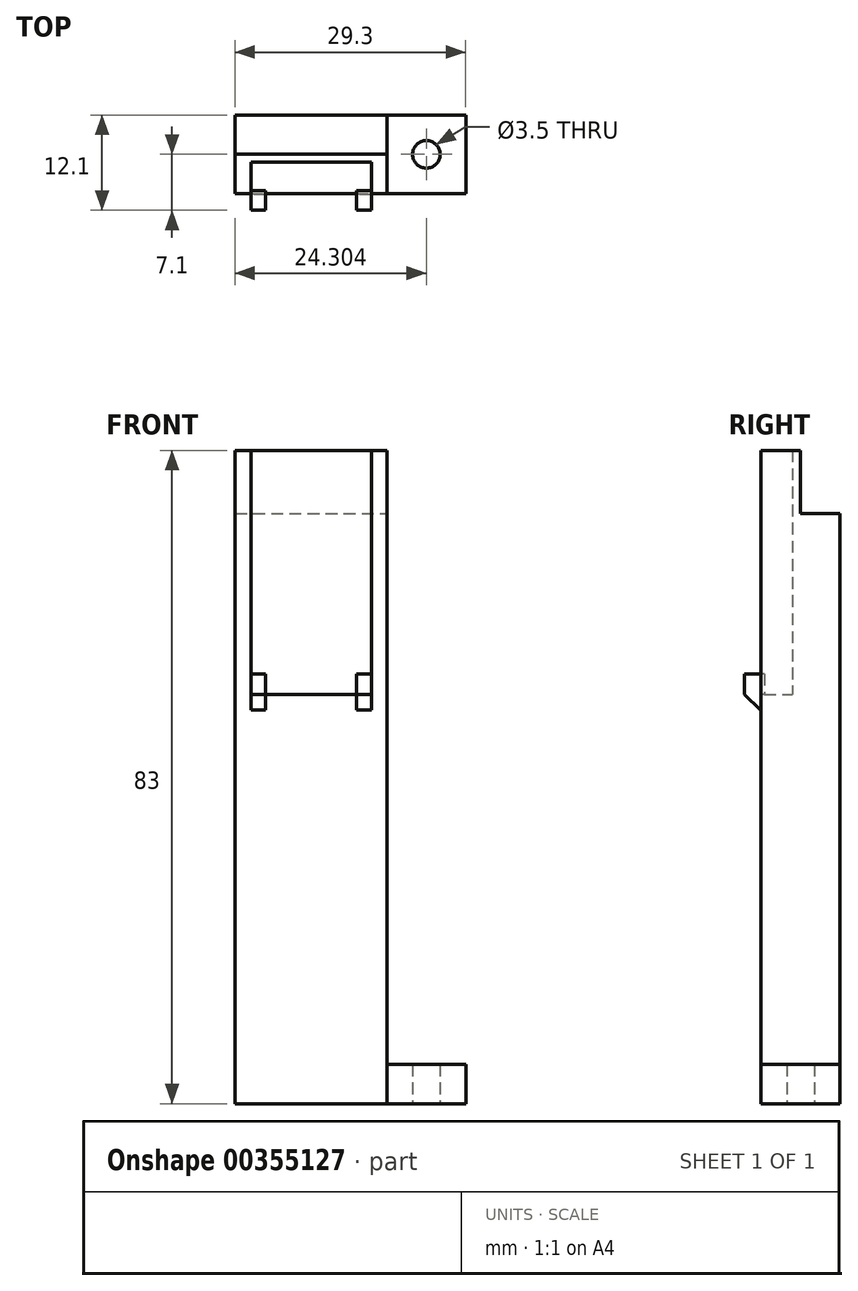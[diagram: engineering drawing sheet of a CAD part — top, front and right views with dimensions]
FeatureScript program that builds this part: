
annotation { "Feature Type Name" : "Feature", "Feature Type Description" : "" }
export const myFeature = defineFeature(function(context is Context, id is Id, definition is map)
    precondition{}
    {
        {
            var Q0;
            Q0=qCreatedBy(makeId("Front.planeOp"),FACE);
            var sketch = newSketch(context, id + "F0", { "sketchPlane" : qUnion([Q0])});
            skLineSegment(sketch, "E0.bottom", {"start": v(-6.93, -11.62) * mm, "end": v(8.37, -11.62) * mm});
            skLineSegment(sketch, "E0.top", {"start": v(-6.93, -42.62) * mm, "end": v(8.37, -42.62) * mm});
            skLineSegment(sketch, "E0.left", {"start": v(-6.93, -11.62) * mm, "end": v(-6.93, -42.62) * mm});
            skLineSegment(sketch, "E0.right", {"start": v(8.37, -11.62) * mm, "end": v(8.37, -42.62) * mm});
            skLineSegment(sketch, "E1.0", {"start": v(-8.93, -11.62) * mm, "end": v(-8.93, -44.62) * mm});
            skLineSegment(sketch, "E1.1", {"start": v(-8.93, -44.62) * mm, "end": v(10.37, -44.62) * mm});
            skLineSegment(sketch, "E1.2", {"start": v(10.37, -11.62) * mm, "end": v(10.37, -44.62) * mm});
            skLineSegment(sketch, "E2", {"start": v(-8.93, -11.62) * mm, "end": v(-6.93, -11.62) * mm});
            skLineSegment(sketch, "E3", {"start": v(8.37, -11.62) * mm, "end": v(10.37, -11.62) * mm});
            skSolve(sketch);
        }
        {
            var Q0;
            Q0=makeQuery(id+"F0.imprint","IMPRINT",FACE,{"disambiguationData":[TD([[makeQuery(id+"F0.imprint","IMPRINT",EDGE,{"derivedFrom":sQuery(id+"F0.wireOp",EDGE,"E0.bottom")}),-1.0]])]});
            extrude(context, id + "F1", {"entities" : qUnion([Q0]), "depth" : 1 * mm});
        }
        {
            var Q0;
            Q0=makeQuery(id+"F0.imprint","IMPRINT",FACE,{"disambiguationData":[TD([[makeQuery(id+"F0.imprint","IMPRINT",EDGE,{"derivedFrom":sQuery(id+"F0.wireOp",EDGE,"E0.top")}),-1.0]])]});
            extrude(context, id + "F2", {"entities" : qUnion([Q0]), "operationType" : NewBodyOperationType.ADD, "depth" : 5 * mm});
        }
        {
            var Q0;
            Q0=makeQuery(id+"F2.opExtrude","SWEPT_FACE",FACE,{"disambiguationData":[OSD([sQuery(id+"F0.wireOp",EDGE,"E0.top")])]});
            var sketch = newSketch(context, id + "F3", { "sketchPlane" : qUnion([Q0])});
            skLineSegment(sketch, "E4", {"start": v(0.72, -5) * mm, "end": v(0.72, -1) * mm, "construction": true});
            skLineSegment(sketch, "E5.bottom", {"start": v(8.37, -4.6) * mm, "end": v(6.47, -4.6) * mm});
            skLineSegment(sketch, "E5.top", {"start": v(8.37, -7.1) * mm, "end": v(6.47, -7.1) * mm});
            skLineSegment(sketch, "E5.left", {"start": v(8.37, -4.6) * mm, "end": v(8.37, -7.1) * mm});
            skLineSegment(sketch, "E5.right", {"start": v(6.47, -4.6) * mm, "end": v(6.47, -7.1) * mm});
            skLineSegment(sketch, "E6.MirrorCS", {"start": v(-5.03, -4.6) * mm, "end": v(-5.03, -7.1) * mm});
            skLineSegment(sketch, "E7.MirrorCS", {"start": v(-6.93, -4.6) * mm, "end": v(-5.03, -4.6) * mm});
            skLineSegment(sketch, "E8.MirrorCS", {"start": v(-6.93, -4.6) * mm, "end": v(-6.93, -7.1) * mm});
            skLineSegment(sketch, "E9.MirrorCS", {"start": v(-6.93, -7.1) * mm, "end": v(-5.03, -7.1) * mm});
            skSolve(sketch);
        }
        {
            var Q0;
            {var subQ0=sQuery(id+"F3.wireOp",EDGE,"E9.MirrorCS");Q0=makeQuery(id+"F3.imprint","IMPRINT",FACE,{"disambiguationData":[TD([[makeQuery(id+"F3.imprint","IMPRINT",EDGE,{"derivedFrom":subQ0}),1.0]])]});}
            var Q1;
            {var subQ0=sQuery(id+"F3.wireOp",EDGE,"E7.MirrorCS");Q1=makeQuery(id+"F3.imprint","IMPRINT",FACE,{"disambiguationData":[TD([[makeQuery(id+"F3.imprint","IMPRINT",EDGE,{"derivedFrom":subQ0}),-1.0]])]});}
            var Q2;
            {var subQ0=sQuery(id+"F3.wireOp",EDGE,"E5.top");Q2=makeQuery(id+"F3.imprint","IMPRINT",FACE,{"disambiguationData":[TD([[makeQuery(id+"F3.imprint","IMPRINT",EDGE,{"derivedFrom":subQ0}),-1.0]])]});}
            var Q3;
            {var subQ0=sQuery(id+"F3.wireOp",EDGE,"E5.bottom");Q3=makeQuery(id+"F3.imprint","IMPRINT",FACE,{"disambiguationData":[TD([[makeQuery(id+"F3.imprint","IMPRINT",EDGE,{"derivedFrom":subQ0}),1.0]])]});}
            extrude(context, id + "F4", {"entities" : qUnion([Q0, Q1, Q2, Q3]), "operationType" : NewBodyOperationType.ADD, "depth" : 2.6 * mm});
        }
        {
            var Q0;
            Q0=makeQuery(id+"F2.opExtrude","CAP_FACE",FACE,{"disambiguationData":[OSD([sQuery(id+"F0.wireOp",EDGE,"E0.top"),sQuery(id+"F0.wireOp",EDGE,"E0.left"),sQuery(id+"F0.wireOp",EDGE,"E0.right"),sQuery(id+"F0.wireOp",EDGE,"E1.0"),sQuery(id+"F0.wireOp",EDGE,"E1.1"),sQuery(id+"F0.wireOp",EDGE,"E1.2"),sQuery(id+"F0.wireOp",EDGE,"E2"),sQuery(id+"F0.wireOp",EDGE,"E3")])],"isStart":false});
            var sketch = newSketch(context, id + "F5", { "sketchPlane" : qUnion([Q0])});
            skLineSegment(sketch, "E10.bottom", {"start": v(6.47, -42.62) * mm, "end": v(8.37, -42.62) * mm});
            skLineSegment(sketch, "E10.top", {"start": v(6.47, -44.62) * mm, "end": v(8.37, -44.62) * mm});
            skLineSegment(sketch, "E10.left", {"start": v(6.47, -42.62) * mm, "end": v(6.47, -44.62) * mm});
            skLineSegment(sketch, "E10.right", {"start": v(8.37, -42.62) * mm, "end": v(8.37, -44.62) * mm});
            skLineSegment(sketch, "E11.bottom", {"start": v(-6.93, -42.62) * mm, "end": v(-5.03, -42.62) * mm});
            skLineSegment(sketch, "E11.top", {"start": v(-6.93, -44.62) * mm, "end": v(-5.03, -44.62) * mm});
            skLineSegment(sketch, "E11.left", {"start": v(-6.93, -42.62) * mm, "end": v(-6.93, -44.62) * mm});
            skLineSegment(sketch, "E11.right", {"start": v(-5.03, -42.62) * mm, "end": v(-5.03, -44.62) * mm});
            skSolve(sketch);
        }
        {
            var Q0;
            Q0=makeQuery(id+"F5.imprint","IMPRINT",FACE,{"disambiguationData":[TD([[makeQuery(id+"F5.imprint","IMPRINT",EDGE,{"derivedFrom":sQuery(id+"F5.wireOp",EDGE,"E11.bottom")}),-1.0]])]});
            var Q1;
            Q1=makeQuery(id+"F5.imprint","IMPRINT",FACE,{"disambiguationData":[TD([[makeQuery(id+"F5.imprint","IMPRINT",EDGE,{"derivedFrom":sQuery(id+"F5.wireOp",EDGE,"E10.bottom")}),-1.0]])]});
            extrude(context, id + "F6", {"entities" : qUnion([Q0, Q1]), "operationType" : NewBodyOperationType.ADD, "depth" : 2.1 * mm});
        }
        {
            var Q0;
            Q0=makeQuery(id+"F6.boolean.opBoolean","MERGE",FACE,{"derivedFrom":[makeQuery(id+"F2.opExtrude","SWEPT_FACE",FACE,{"disambiguationData":[OSD([sQuery(id+"F0.wireOp",EDGE,"E1.1")])]}),makeQuery(id+"F6.opExtrude","SWEPT_FACE",FACE,{"disambiguationData":[OSD([sQuery(id+"F5.wireOp",EDGE,"E10.top")])]}),makeQuery(id+"F6.opExtrude","SWEPT_FACE",FACE,{"disambiguationData":[OSD([sQuery(id+"F5.wireOp",EDGE,"E11.top")])]})]});
            var sketch = newSketch(context, id + "F7", { "sketchPlane" : qUnion([Q0])});
            skLineSegment(sketch, "E12.bottom", {"start": v(-8.93, 5) * mm, "end": v(10.37, 5) * mm});
            skLineSegment(sketch, "E12.top", {"start": v(-8.93, -5) * mm, "end": v(10.37, -5) * mm});
            skLineSegment(sketch, "E12.left", {"start": v(-8.93, 5) * mm, "end": v(-8.93, -5) * mm});
            skLineSegment(sketch, "E12.right", {"start": v(10.37, 5) * mm, "end": v(10.37, -5) * mm});
            skSolve(sketch);
        }
        {
            var Q0;
            {var subQ0=sQuery(id+"F7.wireOp",EDGE,"E12.top");Q0=makeQuery(id+"F7.imprint","IMPRINT",FACE,{"disambiguationData":[TD([[makeQuery(id+"F7.imprint","IMPRINT",EDGE,{"derivedFrom":subQ0}),1.0]])]});}
            var Q1;
            {var subQ2=sQuery(id+"F0.wireOp",EDGE,"E1.1");var subQ12=makeQuery(id+"F2.opExtrude","CAP_EDGE",EDGE,{"disambiguationData":[OSD([subQ2])],"isStart":true});Q1=makeQuery(id+"F7.imprint","IMPRINT",FACE,{"disambiguationData":[TD([[makeQuery(id+"F7.imprint","IMPRINT",EDGE,{"derivedFrom":subQ12}),1.0]])]});}
            extrude(context, id + "F8", {"entities" : qUnion([Q0, Q1]), "operationType" : NewBodyOperationType.ADD, "depth" : 50 * mm});
        }
        {
            var Q0;
            Q0=makeQuery(id+"F6.opExtrude","CAP_EDGE",EDGE,{"disambiguationData":[OSD([sQuery(id+"F5.wireOp",EDGE,"E10.top")])],"isStart":false});
            var Q1;
            Q1=makeQuery(id+"F6.opExtrude","CAP_EDGE",EDGE,{"disambiguationData":[OSD([sQuery(id+"F5.wireOp",EDGE,"E11.top")])],"isStart":false});
            chamfer(context, id + "F9", {"entities" : qUnion([Q0, Q1]), "width" : 2 * mm, "tangentPropagation" : true});
        }
        {
            var Q0;
            Q0=makeQuery(id+"F8.opExtrude","CAP_FACE",FACE,{"disambiguationData":[OSD([sQuery(id+"F7.wireOp",EDGE,"E12.bottom"),sQuery(id+"F7.wireOp",EDGE,"E12.top"),sQuery(id+"F7.wireOp",EDGE,"E12.left"),sQuery(id+"F7.wireOp",EDGE,"E12.right")])],"isStart":true});
            extrude(context, id + "F10", {"entities" : qUnion([Q0]), "operationType" : NewBodyOperationType.ADD, "depth" : 25 * mm});
        }
        {
            var Q0;
            Q0=makeQuery(id+"F8.opExtrude","CAP_FACE",FACE,{"disambiguationData":[OSD([sQuery(id+"F7.wireOp",EDGE,"E12.bottom"),sQuery(id+"F7.wireOp",EDGE,"E12.top"),sQuery(id+"F7.wireOp",EDGE,"E12.left"),sQuery(id+"F7.wireOp",EDGE,"E12.right")])],"isStart":false});
            var sketch = newSketch(context, id + "F11", { "sketchPlane" : qUnion([Q0])});
            skLineSegment(sketch, "E13.bottom", {"start": v(10.37, 5) * mm, "end": v(20.37, 5) * mm});
            skLineSegment(sketch, "E13.top", {"start": v(10.37, -5) * mm, "end": v(20.37, -5) * mm});
            skLineSegment(sketch, "E13.left", {"start": v(10.37, 5) * mm, "end": v(10.37, -5) * mm});
            skLineSegment(sketch, "E13.right", {"start": v(20.37, 5) * mm, "end": v(20.37, -5) * mm});
            skCircle(sketch, "E14", {"center": v(15.37, 0) * mm, "radius": 1.75 * mm});
            skPoint(sketch, "E14.centerSnap0", {"position": v(15.37, -5) * mm});
            skPoint(sketch, "E14.centerSnap1", {"position": v(20.37, 0) * mm});
            skSolve(sketch);
        }
        {
            var Q0;
            Q0=makeQuery(id+"F11.imprint","IMPRINT",FACE,{"disambiguationData":[TD([[makeQuery(id+"F11.imprint","IMPRINT",EDGE,{"derivedFrom":sQuery(id+"F11.wireOp",EDGE,"E13.bottom")}),-1.0]])]});
            extrude(context, id + "F12", {"entities" : qUnion([Q0]), "oppositeDirection" : true, "depth" : 5 * mm});
        }
    });
